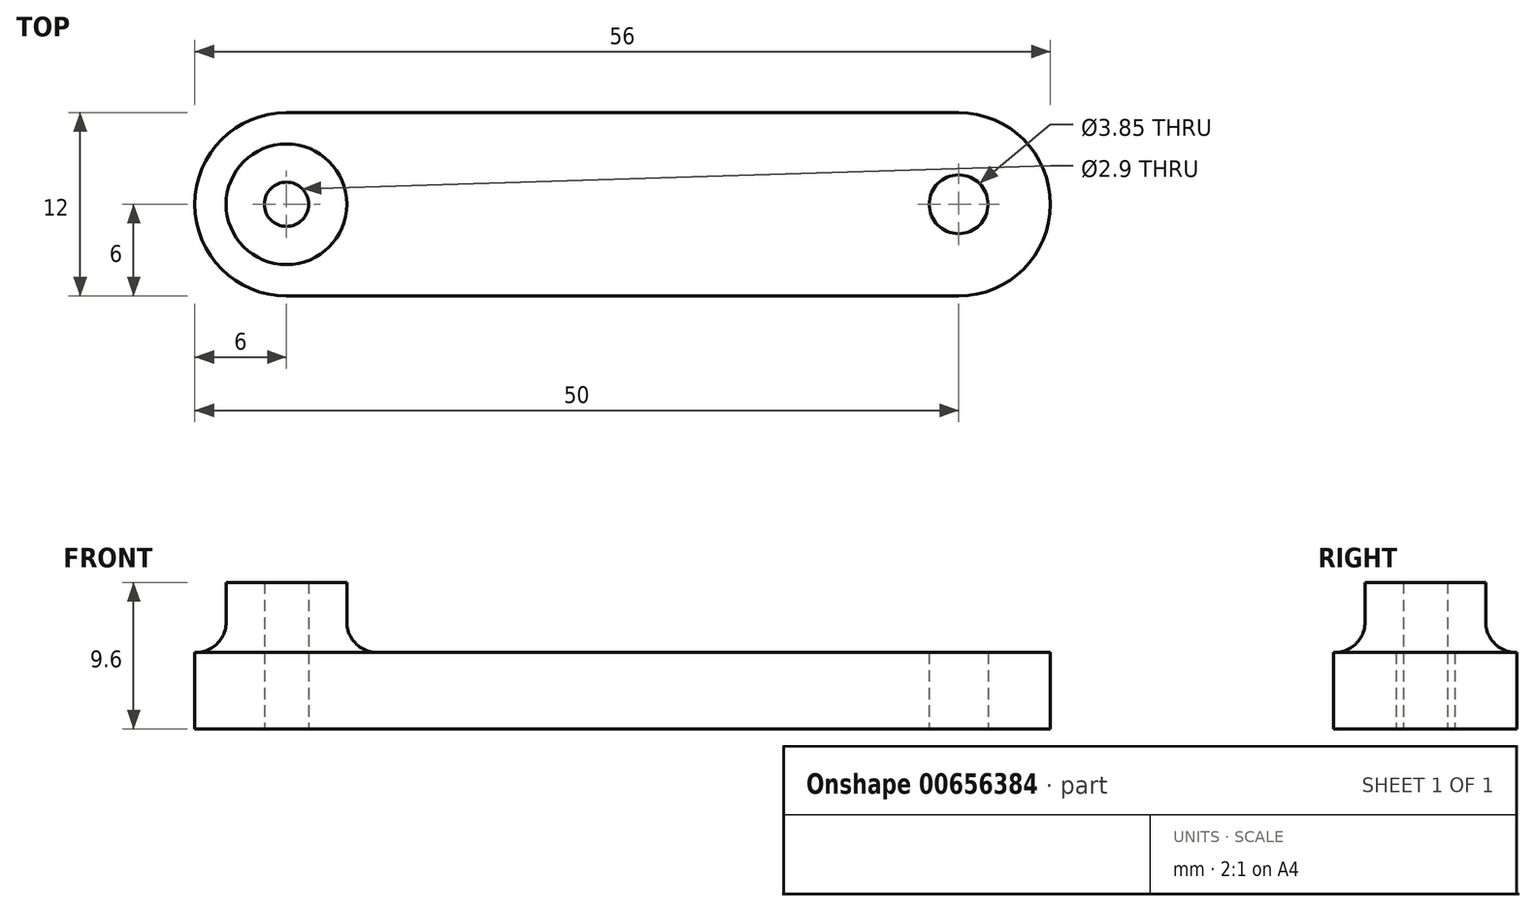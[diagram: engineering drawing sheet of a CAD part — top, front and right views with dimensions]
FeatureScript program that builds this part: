
annotation { "Feature Type Name" : "Feature", "Feature Type Description" : "" }
export const myFeature = defineFeature(function(context is Context, id is Id, definition is map)
    precondition{}
    {
        {
            var Q0;
            Q0=qCreatedBy(makeId("Top.planeOp"),FACE);
            var sketch = newSketch(context, id + "F0", { "sketchPlane" : qUnion([Q0])});
            skArc(sketch, "E0", {"start": v(0, -6) * mm, "mid": v(6, 0) * mm, "end": v(0, 6) * mm});
            skLineSegment(sketch, "E1", {"start": v(0, 6) * mm, "end": v(-44, 6) * mm});
            skLineSegment(sketch, "E2", {"start": v(0, -6) * mm, "end": v(-44, -6) * mm});
            skArc(sketch, "E3", {"start": v(-44, 6) * mm, "mid": v(-50, 0) * mm, "end": v(-44, -6) * mm});
            skCircle(sketch, "E4", {"center": v(-44, 0) * mm, "radius": 1.93 * mm});
            skCircle(sketch, "E5", {"center": v(0, 0) * mm, "radius": 1.93 * mm});
            skSolve(sketch);
        }
        {
            var Q0;
            Q0=qSketchRegion(id+"F0",true);
            extrude(context, id + "F1", {"entities" : qUnion([Q0]), "depth" : 5 * mm});
        }
        {
            var Q0;
            Q0=makeQuery(id+"F1.opExtrude","CAP_FACE",FACE,{"disambiguationData":[OSD([sQuery(id+"F0.wireOp",EDGE,"E0"),sQuery(id+"F0.wireOp",EDGE,"E1"),sQuery(id+"F0.wireOp",EDGE,"E2"),sQuery(id+"F0.wireOp",EDGE,"E3"),sQuery(id+"F0.wireOp",EDGE,"E4"),sQuery(id+"F0.wireOp",EDGE,"E5")])],"isStart":false});
            var sketch = newSketch(context, id + "F2", { "sketchPlane" : qUnion([Q0])});
            skCircle(sketch, "E6", {"center": v(-44, 0) * mm, "radius": 1.45 * mm});
            skCircle(sketch, "E7", {"center": v(-44, 0) * mm, "radius": 3.95 * mm});
            skSolve(sketch);
        }
        {
            var Q0;
            Q0=qSketchRegion(id+"F2",true);
            var Q1;
            Q1=makeQuery(id+"F1.opExtrude","CAP_FACE",FACE,{"disambiguationData":[OSD([sQuery(id+"F0.wireOp",EDGE,"E0"),sQuery(id+"F0.wireOp",EDGE,"E1"),sQuery(id+"F0.wireOp",EDGE,"E2"),sQuery(id+"F0.wireOp",EDGE,"E3"),sQuery(id+"F0.wireOp",EDGE,"E4"),sQuery(id+"F0.wireOp",EDGE,"E5")])],"isStart":true});
            extrude(context, id + "F3", {"entities" : qUnion([Q0]), "operationType" : NewBodyOperationType.ADD, "depth" : 4.6 * mm, "hasSecondDirection" : true, "secondDirectionBound" : SecondDirectionBoundingType.UP_TO_SURFACE, "secondDirectionOppositeDirection" : true, "secondDirectionBoundEntityFace" : qUnion([Q1]), "secondDirectionDepth" : 25 * mm});
        }
        {
            var Q0;
            Q0=makeQuery(id+"F3.boolean.opBoolean","INTERSECT",EDGE,{"derivedFrom":[makeQuery(id+"F1.opExtrude","CAP_FACE",FACE,{"disambiguationData":[OSD([sQuery(id+"F0.wireOp",EDGE,"E0"),sQuery(id+"F0.wireOp",EDGE,"E1"),sQuery(id+"F0.wireOp",EDGE,"E2"),sQuery(id+"F0.wireOp",EDGE,"E3"),sQuery(id+"F0.wireOp",EDGE,"E4"),sQuery(id+"F0.wireOp",EDGE,"E5")])],"isStart":false}),makeQuery(id+"F3.opExtrude","SWEPT_FACE",FACE,{"disambiguationData":[OSD([sQuery(id+"F2.wireOp",EDGE,"E7")])]})]});
            fillet(context, id + "F4", {"entities" : qUnion([Q0]), "radius" : 2 * mm, "tangentPropagation" : true, "allowEdgeOverflow" : false});
        }
    });
